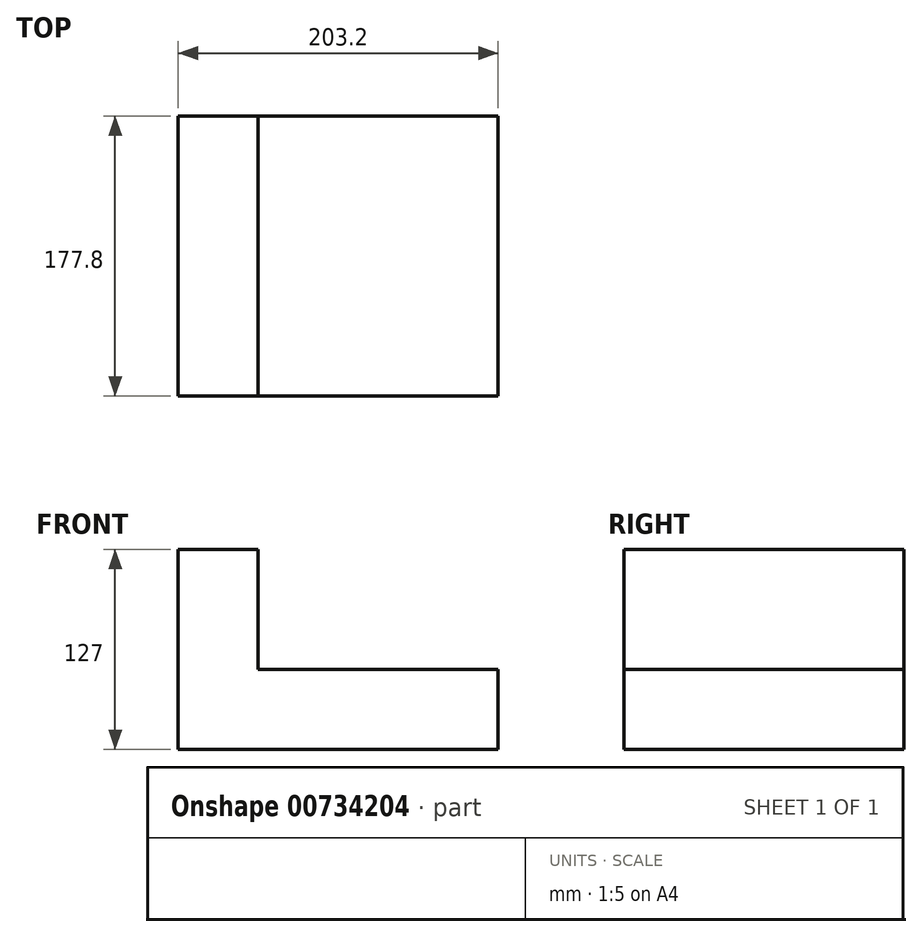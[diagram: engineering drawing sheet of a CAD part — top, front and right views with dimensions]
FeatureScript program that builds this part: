
annotation { "Feature Type Name" : "Feature", "Feature Type Description" : "" }
export const myFeature = defineFeature(function(context is Context, id is Id, definition is map)
    precondition{}
    {
        {
            var Q0;
            Q0=qCreatedBy(makeId("Front.planeOp"),FACE);
            var sketch = newSketch(context, id + "F0", { "sketchPlane" : qUnion([Q0])});
            skLineSegment(sketch, "E0", {"start": v(-48.26, 166.3) * mm, "end": v(-48.26, 39.3) * mm});
            skLineSegment(sketch, "E1", {"start": v(-48.26, 39.3) * mm, "end": v(154.94, 39.3) * mm});
            skLineSegment(sketch, "E2", {"start": v(154.94, 39.3) * mm, "end": v(154.94, 90.1) * mm});
            skLineSegment(sketch, "E3", {"start": v(154.94, 90.1) * mm, "end": v(2.54, 90.1) * mm});
            skLineSegment(sketch, "E4", {"start": v(2.54, 90.1) * mm, "end": v(2.54, 166.3) * mm});
            skLineSegment(sketch, "E5", {"start": v(2.54, 166.3) * mm, "end": v(-48.26, 166.3) * mm});
            skSolve(sketch);
        }
        {
            var Q0;
            Q0=makeQuery(id+"F0.imprint","IMPRINT",FACE,{"disambiguationData":[TD([[makeQuery(id+"F0.imprint","IMPRINT",EDGE,{"derivedFrom":sQuery(id+"F0.wireOp",EDGE,"E0")}),1.0]])]});
            extrude(context, id + "F1", {"entities" : qUnion([Q0]), "depth" : 177.8 * mm, "offsetDistance" : 25.4 * mm});
        }
    });
